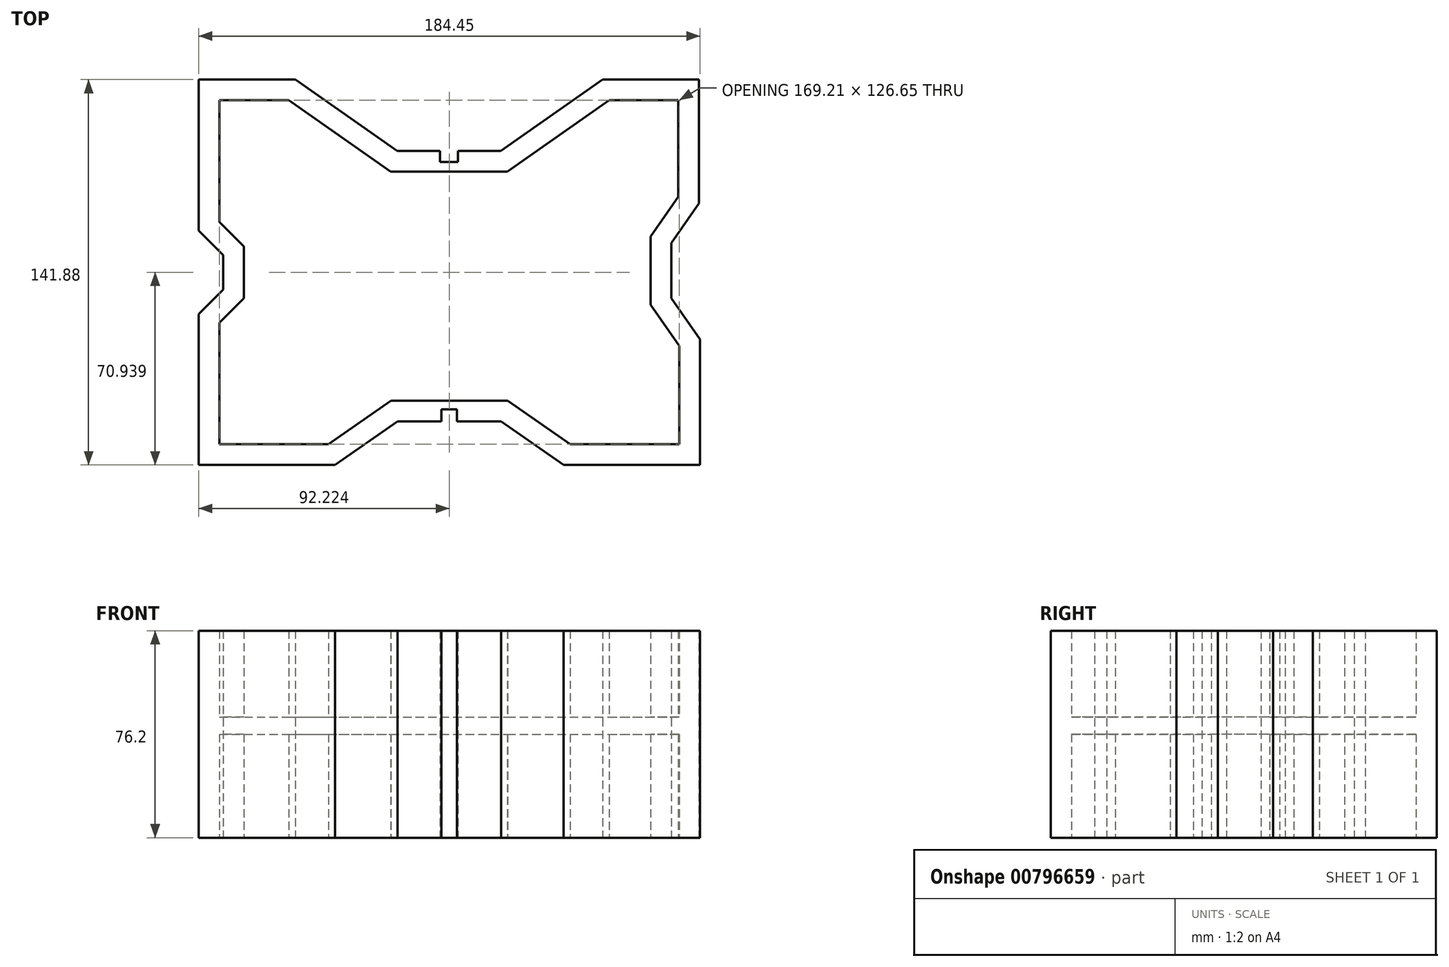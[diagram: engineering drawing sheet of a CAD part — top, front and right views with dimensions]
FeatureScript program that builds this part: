
annotation { "Feature Type Name" : "Feature", "Feature Type Description" : "" }
export const myFeature = defineFeature(function(context is Context, id is Id, definition is map)
    precondition{}
    {
        {
            var Q0;
            Q0=qCreatedBy(makeId("Top.planeOp"),FACE);
            var sketch = newSketch(context, id + "F0", { "sketchPlane" : qUnion([Q0])});
            skLineSegment(sketch, "E0", {"start": v(-83.18, 6.05) * mm, "end": v(-92.16, -2.93) * mm});
            skLineSegment(sketch, "E1", {"start": v(-92.16, -2.93) * mm, "end": v(-92.16, -58.5) * mm});
            skLineSegment(sketch, "E2", {"start": v(-92.16, -58.5) * mm, "end": v(-42.02, -58.5) * mm});
            skLineSegment(sketch, "E3", {"start": v(-42.02, -58.5) * mm, "end": v(-19.05, -42.42) * mm});
            skLineSegment(sketch, "E4", {"start": v(-19.05, -42.42) * mm, "end": v(-2.86, -42.42) * mm});
            skLineSegment(sketch, "E5", {"start": v(19.05, -42.42) * mm, "end": v(42.02, -58.5) * mm});
            skLineSegment(sketch, "E6", {"start": v(42.02, -58.5) * mm, "end": v(92.29, -58.5) * mm});
            skLineSegment(sketch, "E7", {"start": v(92.29, -58.5) * mm, "end": v(92.29, -12.28) * mm});
            skLineSegment(sketch, "E8", {"start": v(92.29, -12.28) * mm, "end": v(81.64, 2.93) * mm});
            skPoint(sketch, "E9", {"position": v(0, -42.42) * mm});
            skLineSegment(sketch, "E10.MirrorCS", {"start": v(-19.15, 57.16) * mm, "end": v(-3.36, 57.16) * mm});
            skLineSegment(sketch, "E11.MirrorCS", {"start": v(-56.6, 83.38) * mm, "end": v(-19.15, 57.16) * mm});
            skLineSegment(sketch, "E12.MirrorCS", {"start": v(-92.16, 83.38) * mm, "end": v(-56.6, 83.38) * mm});
            skLineSegment(sketch, "E13.MirrorCS", {"start": v(-92.16, 27.73) * mm, "end": v(-92.16, 83.38) * mm});
            skLineSegment(sketch, "E14.MirrorCS", {"start": v(-83.18, 18.75) * mm, "end": v(-92.16, 27.73) * mm});
            skLineSegment(sketch, "E15.MirrorCS", {"start": v(91.84, 37.81) * mm, "end": v(81.64, 23.25) * mm});
            skLineSegment(sketch, "E16.MirrorCS", {"start": v(91.84, 83.38) * mm, "end": v(91.84, 37.81) * mm});
            skLineSegment(sketch, "E17.MirrorCS", {"start": v(56.4, 83.38) * mm, "end": v(91.84, 83.38) * mm});
            skLineSegment(sketch, "E18.MirrorCS", {"start": v(18.95, 57.16) * mm, "end": v(56.4, 83.38) * mm});
            skLineSegment(sketch, "E19", {"start": v(-83.18, 18.75) * mm, "end": v(-83.18, 6.05) * mm});
            skLineSegment(sketch, "E20", {"start": v(81.64, 23.25) * mm, "end": v(81.64, 2.93) * mm});
            skPoint(sketch, "E21", {"position": v(-83.18, 12.4) * mm});
            skLineSegment(sketch, "E22.0", {"start": v(-84.54, 75.76) * mm, "end": v(-59, 75.76) * mm});
            skLineSegment(sketch, "E22.1", {"start": v(-84.54, 30.89) * mm, "end": v(-84.54, 75.76) * mm});
            skLineSegment(sketch, "E22.2", {"start": v(-75.56, 21.9) * mm, "end": v(-84.54, 30.89) * mm});
            skLineSegment(sketch, "E22.3", {"start": v(-75.56, 21.9) * mm, "end": v(-75.56, 2.9) * mm});
            skLineSegment(sketch, "E22.4", {"start": v(-75.56, 2.9) * mm, "end": v(-84.54, -6.09) * mm});
            skLineSegment(sketch, "E22.5", {"start": v(-59, 75.76) * mm, "end": v(-21.55, 49.54) * mm});
            skLineSegment(sketch, "E22.6", {"start": v(-84.54, -6.09) * mm, "end": v(-84.54, -50.88) * mm});
            skLineSegment(sketch, "E22.7", {"start": v(-84.54, -50.88) * mm, "end": v(-44.42, -50.88) * mm});
            skLineSegment(sketch, "E22.8", {"start": v(-44.42, -50.88) * mm, "end": v(-21.45, -34.8) * mm});
            skLineSegment(sketch, "E22.9", {"start": v(-21.45, -34.8) * mm, "end": v(21.45, -34.8) * mm});
            skLineSegment(sketch, "E22.10", {"start": v(84.22, 75.76) * mm, "end": v(84.22, 40.22) * mm});
            skLineSegment(sketch, "E22.11", {"start": v(58.8, 75.76) * mm, "end": v(84.22, 75.76) * mm});
            skLineSegment(sketch, "E22.12", {"start": v(21.35, 49.54) * mm, "end": v(58.8, 75.76) * mm});
            skLineSegment(sketch, "E22.13", {"start": v(-21.55, 49.54) * mm, "end": v(21.35, 49.54) * mm});
            skLineSegment(sketch, "E22.14", {"start": v(84.22, 40.22) * mm, "end": v(74.02, 25.65) * mm});
            skLineSegment(sketch, "E22.15", {"start": v(74.02, 25.65) * mm, "end": v(74.02, 0.53) * mm});
            skLineSegment(sketch, "E22.16", {"start": v(84.67, -14.68) * mm, "end": v(74.02, 0.53) * mm});
            skLineSegment(sketch, "E22.17", {"start": v(84.67, -50.88) * mm, "end": v(84.67, -14.68) * mm});
            skLineSegment(sketch, "E22.18", {"start": v(44.42, -50.88) * mm, "end": v(84.67, -50.88) * mm});
            skLineSegment(sketch, "E22.19", {"start": v(21.45, -34.8) * mm, "end": v(44.42, -50.88) * mm});
            skLineSegment(sketch, "E23.top", {"start": v(-3.36, 53.1) * mm, "end": v(3.22, 53.1) * mm});
            skLineSegment(sketch, "E23.left", {"start": v(-3.36, 57.16) * mm, "end": v(-3.36, 53.1) * mm});
            skLineSegment(sketch, "E23.right", {"start": v(3.22, 57.16) * mm, "end": v(3.22, 53.1) * mm});
            skLineSegment(sketch, "E24.trimOffspring", {"start": v(3.22, 57.16) * mm, "end": v(18.95, 57.16) * mm});
            skLineSegment(sketch, "E25.top", {"start": v(-2.86, -38) * mm, "end": v(2.86, -38) * mm});
            skLineSegment(sketch, "E25.left", {"start": v(-2.86, -42.42) * mm, "end": v(-2.86, -38) * mm});
            skLineSegment(sketch, "E25.right", {"start": v(2.86, -42.42) * mm, "end": v(2.86, -38) * mm});
            skLineSegment(sketch, "E26.trimOffspring", {"start": v(2.86, -42.42) * mm, "end": v(19.05, -42.42) * mm});
            skSolve(sketch);
        }
        {
            var Q0;
            Q0=makeQuery(id+"F0.imprint","IMPRINT",FACE,{"disambiguationData":[TD([[makeQuery(id+"F0.imprint","IMPRINT",EDGE,{"derivedFrom":sQuery(id+"F0.wireOp",EDGE,"E0")}),1.0]])]});
            extrude(context, id + "F1", {"entities" : qUnion([Q0]), "endBound" : BoundingType.SYMMETRIC, "depth" : 76.2 * mm, "offsetDistance" : 25.4 * mm});
        }
        {
            var Q0;
            Q0=makeQuery(id+"F0.imprint","IMPRINT",FACE,{"disambiguationData":[TD([[makeQuery(id+"F0.imprint","IMPRINT",EDGE,{"derivedFrom":sQuery(id+"F0.wireOp",EDGE,"E22.0")}),-1.0]])]});
            extrude(context, id + "F2", {"entities" : qUnion([Q0]), "operationType" : NewBodyOperationType.ADD, "depth" : 6.35 * mm, "offsetDistance" : 25.4 * mm});
        }
    });
